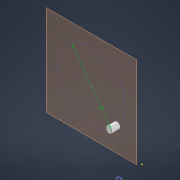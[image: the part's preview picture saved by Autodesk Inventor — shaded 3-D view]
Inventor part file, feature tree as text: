
AUTODESK INVENTOR PART (.ipt)
format: ipt  version: 2022 (Build 260153070, 153G)  size: 98,304 bytes
history: native  units: mm
features: other x5, sketch x2, extrude x1
ambient origin geometry x8: Origin, YZ Plane, XZ Plane, XY Plane, X Axis, Y Axis, Z Axis, Center Point
bodies: Body1 (feature_tree)
feature tree (8):
  other  "Твердое тело1"
  extrude  "Выдавливание1"  Depth=8.0mm
  other  "РабПлоскость1"
  sketch  "Эскиз2"
  sketch  "Эскиз1"
  other  "<userpath>\Documents\Inventor\TUTO\MELAS\Workspace\Twitter.iam"
  other  "Twitter.iam"
  other  "Фланец:1"
